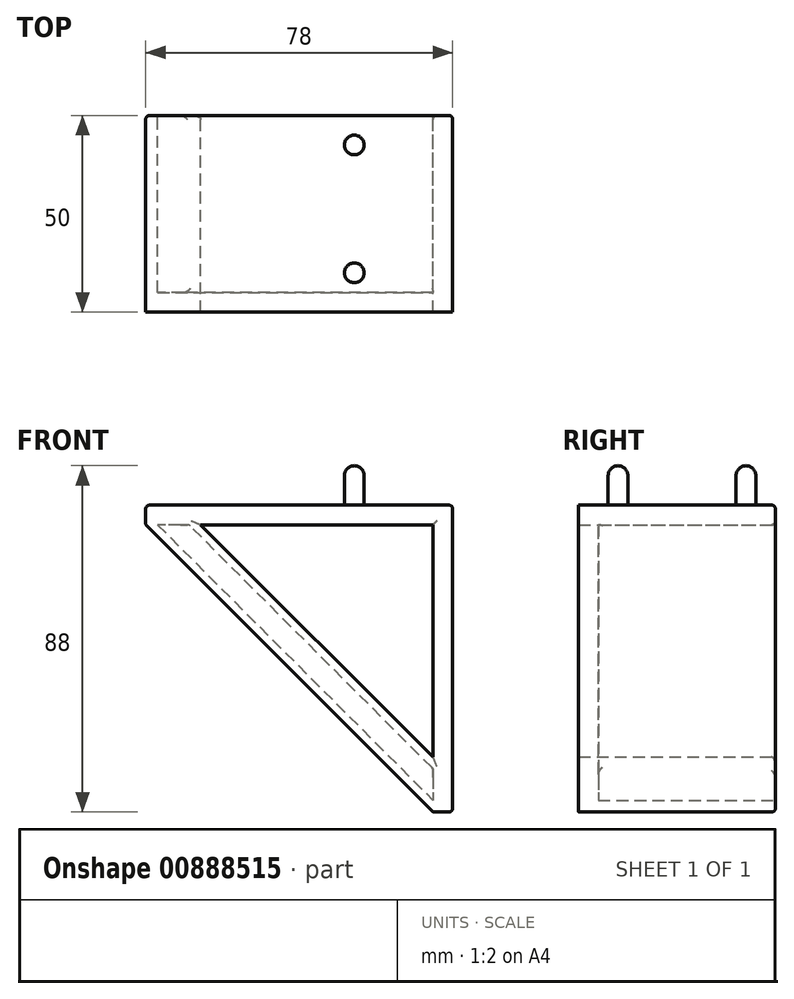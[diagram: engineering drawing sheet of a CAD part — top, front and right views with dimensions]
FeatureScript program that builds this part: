
annotation { "Feature Type Name" : "Feature", "Feature Type Description" : "" }
export const myFeature = defineFeature(function(context is Context, id is Id, definition is map)
    precondition{}
    {
        {
            var Q0;
            Q0=qCreatedBy(makeId("Top.planeOp"),FACE);
            var sketch = newSketch(context, id + "F0", { "sketchPlane" : qUnion([Q0])});
            skLineSegment(sketch, "E0.bottom", {"start": v(-26.48, 25.07) * mm, "end": v(51.52, 25.07) * mm});
            skLineSegment(sketch, "E0.top", {"start": v(-26.48, -24.93) * mm, "end": v(51.52, -24.93) * mm});
            skLineSegment(sketch, "E0.left", {"start": v(-26.48, 25.07) * mm, "end": v(-26.48, -24.93) * mm});
            skLineSegment(sketch, "E0.right", {"start": v(51.52, 25.07) * mm, "end": v(51.52, -24.93) * mm});
            skSolve(sketch);
        }
        {
            var Q0;
            Q0=makeQuery(id+"F0.imprint","IMPRINT",FACE,{"disambiguationData":[TD([[makeQuery(id+"F0.imprint","IMPRINT",EDGE,{"derivedFrom":sQuery(id+"F0.wireOp",EDGE,"E0.bottom")}),-1.0]])]});
            extrude(context, id + "F1", {"entities" : qUnion([Q0]), "depth" : 5 * mm, "offsetDistance" : 25 * mm});
        }
        {
            var Q0;
            Q0=makeQuery(id+"F1.opExtrude","CAP_FACE",FACE,{"disambiguationData":[OSD([sQuery(id+"F0.wireOp",EDGE,"E0.bottom"),sQuery(id+"F0.wireOp",EDGE,"E0.top"),sQuery(id+"F0.wireOp",EDGE,"E0.left"),sQuery(id+"F0.wireOp",EDGE,"E0.right")])],"isStart":false});
            var sketch = newSketch(context, id + "F2", { "sketchPlane" : qUnion([Q0])});
            skCircle(sketch, "E1", {"center": v(26.52, 17.57) * mm, "radius": 2.5 * mm});
            skCircle(sketch, "E2", {"center": v(26.52, -14.93) * mm, "radius": 2.5 * mm});
            skSolve(sketch);
        }
        {
            var Q0;
            Q0=makeQuery(id+"F2.imprint","IMPRINT",FACE,{"disambiguationData":[TD([[makeQuery(id+"F2.imprint","IMPRINT",EDGE,{"derivedFrom":sQuery(id+"F2.wireOp",EDGE,"E1")}),1.0]])]});
            var Q1;
            Q1=makeQuery(id+"F2.imprint","IMPRINT",FACE,{"disambiguationData":[TD([[makeQuery(id+"F2.imprint","IMPRINT",EDGE,{"derivedFrom":sQuery(id+"F2.wireOp",EDGE,"E2")}),1.0]])]});
            extrude(context, id + "F3", {"entities" : qUnion([Q0, Q1]), "operationType" : NewBodyOperationType.ADD, "depth" : 10 * mm, "offsetDistance" : 25 * mm});
        }
        {
            var Q0;
            Q0=makeQuery(id+"F3.opExtrude","CAP_EDGE",EDGE,{"disambiguationData":[OSD([sQuery(id+"F2.wireOp",EDGE,"E1")])],"isStart":false});
            var Q1;
            Q1=makeQuery(id+"F3.opExtrude","CAP_EDGE",EDGE,{"disambiguationData":[OSD([sQuery(id+"F2.wireOp",EDGE,"E2")])],"isStart":false});
            fillet(context, id + "F4", {"entities" : qUnion([Q0, Q1]), "radius" : 2.5 * mm, "tangentPropagation" : true, "allowEdgeOverflow" : false});
        }
        {
            var Q0;
            Q0=makeQuery(id+"F1.opExtrude","SWEPT_FACE",FACE,{"disambiguationData":[OSD([sQuery(id+"F0.wireOp",EDGE,"E0.right")])]});
            var sketch = newSketch(context, id + "F5", { "sketchPlane" : qUnion([Q0])});
            skLineSegment(sketch, "E3.bottom", {"start": v(25.07, 5) * mm, "end": v(-24.93, 5) * mm});
            skLineSegment(sketch, "E3.top", {"start": v(25.07, -73) * mm, "end": v(-24.93, -73) * mm});
            skLineSegment(sketch, "E3.left", {"start": v(25.07, 5) * mm, "end": v(25.07, -73) * mm});
            skLineSegment(sketch, "E3.right", {"start": v(-24.93, 5) * mm, "end": v(-24.93, -73) * mm});
            skSolve(sketch);
        }
        {
            var Q0;
            Q0 = qSketchRegion(id + "F5", true);
            extrude(context, id + "F6", {"entities" : qUnion([Q0]), "operationType" : NewBodyOperationType.ADD, "oppositeDirection" : true, "depth" : 5 * mm, "offsetDistance" : 25 * mm});
        }
        {
            var Q0;
            Q0=makeQuery(id+"F6.boolean.opBoolean","MERGE",FACE,{"derivedFrom":[makeQuery(id+"F1.opExtrude","SWEPT_FACE",FACE,{"disambiguationData":[OSD([sQuery(id+"F0.wireOp",EDGE,"E0.bottom")])]}),makeQuery(id+"F6.opExtrude","SWEPT_FACE",FACE,{"disambiguationData":[OSD([sQuery(id+"F5.wireOp",EDGE,"E3.left")])]})]});
            var sketch = newSketch(context, id + "F7", { "sketchPlane" : qUnion([Q0])});
            skLineSegment(sketch, "E4", {"start": v(26.48, 0) * mm, "end": v(-46.52, -73) * mm});
            skLineSegment(sketch, "E5", {"start": v(12.48, 0) * mm, "end": v(-46.52, -59) * mm});
            skSolve(sketch);
        }
        {
            var Q0;
            {var subQ0=sQuery(id+"F7.wireOp",EDGE,"E4");Q0=makeQuery(id+"F7.imprint","IMPRINT",FACE,{"disambiguationData":[TD([[makeQuery(id+"F7.imprint","IMPRINT",EDGE,{"derivedFrom":subQ0}),-1.0]])]});}
            extrude(context, id + "F8", {"entities" : qUnion([Q0]), "operationType" : NewBodyOperationType.ADD, "oppositeDirection" : true, "depth" : 50 * mm, "offsetDistance" : 25 * mm});
        }
        {
            var Q0;
            {var subQ0=sQuery(id+"F5.wireOp",EDGE,"E3.left");var subQ1=sQuery(id+"F0.wireOp",EDGE,"E0.bottom");Q0=makeQuery(id+"F8.boolean.opBoolean","MERGE",FACE,{"derivedFrom":[makeQuery(id+"F6.boolean.opBoolean","MERGE",FACE,{"derivedFrom":[makeQuery(id+"F1.opExtrude","SWEPT_FACE",FACE,{"disambiguationData":[OSD([subQ1])]}),makeQuery(id+"F6.opExtrude","SWEPT_FACE",FACE,{"disambiguationData":[OSD([subQ0])]})]}),makeQuery(id+"F8.opExtrude","CAP_FACE",FACE,{"disambiguationData":[OSD([subQ1,subQ0,sQuery(id+"F7.wireOp",EDGE,"E4"),sQuery(id+"F7.wireOp",EDGE,"E5")])],"isStart":true})]});}
            var sketch = newSketch(context, id + "F9", { "sketchPlane" : qUnion([Q0])});
            skLineSegment(sketch, "E6", {"start": v(-46.52, -59) * mm, "end": v(-46.52, -73) * mm});
            skLineSegment(sketch, "E7", {"start": v(12.48, 0) * mm, "end": v(26.48, 0) * mm});
            skLineSegment(sketch, "E8", {"start": v(23.48, 0) * mm, "end": v(-46.52, -70) * mm});
            skLineSegment(sketch, "E9", {"start": v(-46.52, -62) * mm, "end": v(15.48, 0) * mm});
            skSolve(sketch);
        }
        {
            var Q0;
            {var subQ0=sQuery(id+"F9.wireOp",EDGE,"E8");Q0=makeQuery(id+"F9.imprint","IMPRINT",FACE,{"disambiguationData":[TD([[makeQuery(id+"F9.imprint","IMPRINT",EDGE,{"derivedFrom":subQ0}),-1.0]])]});}
            extrude(context, id + "F10", {"entities" : qUnion([Q0]), "operationType" : NewBodyOperationType.REMOVE, "oppositeDirection" : true, "depth" : 45 * mm, "offsetDistance" : 25 * mm});
        }
        {
            var Q0;
            Q0=makeQuery(id+"F1.opExtrude","CAP_EDGE",EDGE,{"disambiguationData":[OSD([sQuery(id+"F0.wireOp",EDGE,"E0.bottom")])],"isStart":true});
            var Q1;
            Q1=makeQuery(id+"F6.opExtrude","CAP_EDGE",EDGE,{"disambiguationData":[OSD([sQuery(id+"F5.wireOp",EDGE,"E3.left")])],"isStart":false});
            var Q2;
            Q2=makeQuery(id+"F8.opExtrude","CAP_EDGE",EDGE,{"disambiguationData":[OSD([sQuery(id+"F7.wireOp",EDGE,"E5")])],"isStart":true});
            var Q3;
            Q3=makeQuery(id+"F10.boolean.opBoolean","COPY",FACE,{"derivedFrom":makeQuery(id+"F10.opExtrude","SWEPT_FACE",FACE,{"disambiguationData":[OSD([sQuery(id+"F9.wireOp",EDGE,"E9")])]})});
            var Q4;
            Q4=makeQuery(id+"F1.opExtrude","CAP_EDGE",EDGE,{"disambiguationData":[OSD([sQuery(id+"F0.wireOp",EDGE,"E0.bottom")])],"isStart":false});
            var Q5;
            Q5=makeQuery(id+"F6.boolean.opBoolean","MERGE",EDGE,{"derivedFrom":[makeQuery(id+"F1.opExtrude","SWEPT_EDGE",EDGE,{"disambiguationData":[OSD([sQuery(id+"F0.wireOp",EDGE,"E0.bottom"),sQuery(id+"F0.wireOp",EDGE,"E0.right")])]}),makeQuery(id+"F6.opExtrude","CAP_EDGE",EDGE,{"disambiguationData":[OSD([sQuery(id+"F5.wireOp",EDGE,"E3.left")])],"isStart":true})]});
            var Q6;
            Q6=makeQuery(id+"F6.opExtrude","SWEPT_EDGE",EDGE,{"disambiguationData":[OSD([sQuery(id+"F5.wireOp",EDGE,"E3.top"),sQuery(id+"F5.wireOp",EDGE,"E3.left")])]});
            var Q7;
            Q7=makeQuery(id+"F8.opExtrude","CAP_EDGE",EDGE,{"disambiguationData":[OSD([sQuery(id+"F7.wireOp",EDGE,"E4")])],"isStart":true});
            var Q8;
            Q8=makeQuery(id+"F1.opExtrude","SWEPT_EDGE",EDGE,{"disambiguationData":[OSD([sQuery(id+"F0.wireOp",EDGE,"E0.bottom"),sQuery(id+"F0.wireOp",EDGE,"E0.left")])]});
            var Q9;
            Q9=makeQuery(id+"F10.boolean.opBoolean","COPY",EDGE,{"derivedFrom":makeQuery(id+"F10.opExtrude","CAP_EDGE",EDGE,{"disambiguationData":[OSD([sQuery(id+"F9.wireOp",EDGE,"E8")])],"isStart":true})});
            var Q10;
            Q10=makeQuery(id+"F6.opExtrude","CAP_EDGE",EDGE,{"disambiguationData":[OSD([sQuery(id+"F5.wireOp",EDGE,"E3.top")])],"isStart":true});
            var Q11;
            {var subQ0=sQuery(id+"F5.wireOp",EDGE,"E3.top");Q11=makeQuery(id+"F8.boolean.opBoolean","MERGE",EDGE,{"derivedFrom":[makeQuery(id+"F6.opExtrude","CAP_EDGE",EDGE,{"disambiguationData":[OSD([subQ0])],"isStart":false}),makeQuery(id+"F8.opExtrude","SWEPT_EDGE",EDGE,{"disambiguationData":[OSD([subQ0,sQuery(id+"F5.wireOp",EDGE,"E3.left"),sQuery(id+"F7.wireOp",EDGE,"E4")])]})]});}
            var Q12;
            Q12=makeQuery(id+"F1.opExtrude","CAP_EDGE",EDGE,{"disambiguationData":[OSD([sQuery(id+"F0.wireOp",EDGE,"E0.right")])],"isStart":false});
            var Q13;
            {var subQ0=sQuery(id+"F0.wireOp",EDGE,"E0.left");Q13=makeQuery(id+"F8.boolean.opBoolean","MERGE",EDGE,{"derivedFrom":[makeQuery(id+"F1.opExtrude","CAP_EDGE",EDGE,{"disambiguationData":[OSD([subQ0])],"isStart":true}),makeQuery(id+"F8.opExtrude","SWEPT_EDGE",EDGE,{"disambiguationData":[OSD([sQuery(id+"F0.wireOp",EDGE,"E0.bottom"),subQ0,sQuery(id+"F7.wireOp",EDGE,"E4")])]})]});}
            var Q14;
            Q14=makeQuery(id+"F1.opExtrude","CAP_EDGE",EDGE,{"disambiguationData":[OSD([sQuery(id+"F0.wireOp",EDGE,"E0.left")])],"isStart":false});
            fillet(context, id + "F11", {"entities" : qUnion([Q0, Q1, Q2, Q3, Q4, Q5, Q6, Q7, Q8, Q9, Q10, Q11, Q12, Q13, Q14]), "radius" : 1 * mm, "tangentPropagation" : true, "allowEdgeOverflow" : false});
        }
    });
